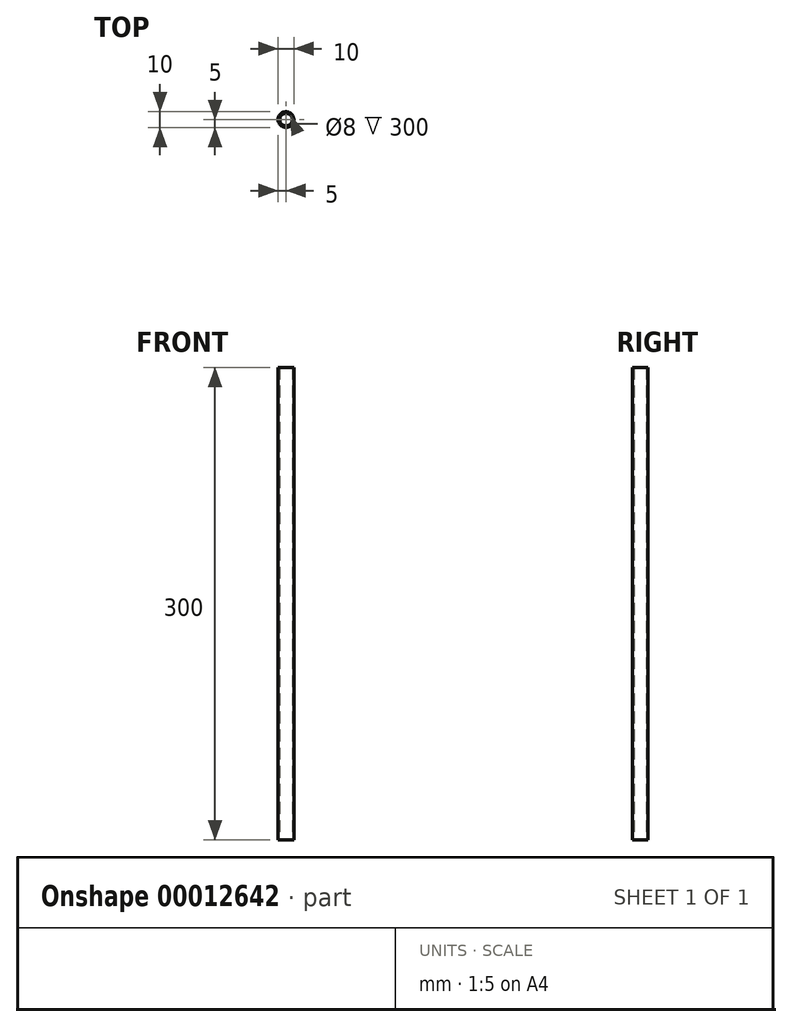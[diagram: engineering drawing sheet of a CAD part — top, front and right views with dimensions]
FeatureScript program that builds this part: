
annotation { "Feature Type Name" : "Feature", "Feature Type Description" : "" }
export const myFeature = defineFeature(function(context is Context, id is Id, definition is map)
    precondition{}
    {
        {
            var Q0;
            Q0=qCreatedBy(makeId("Top.planeOp"),FACE);
            var sketch = newSketch(context, id + "F0", { "sketchPlane" : qUnion([Q0])});
            skCircle(sketch, "E0", {"center": v(0, 0) * mm, "radius": 4 * mm});
            skCircle(sketch, "E1.0", {"center": v(0, 0) * mm, "radius": 5 * mm});
            skSolve(sketch);
        }
        {
            var Q0;
            Q0 = qSketchRegion(id + "F0", true);
            extrude(context, id + "F1", {"entities" : qUnion([Q0]), "depth" : 300 * mm});
        }
    });
